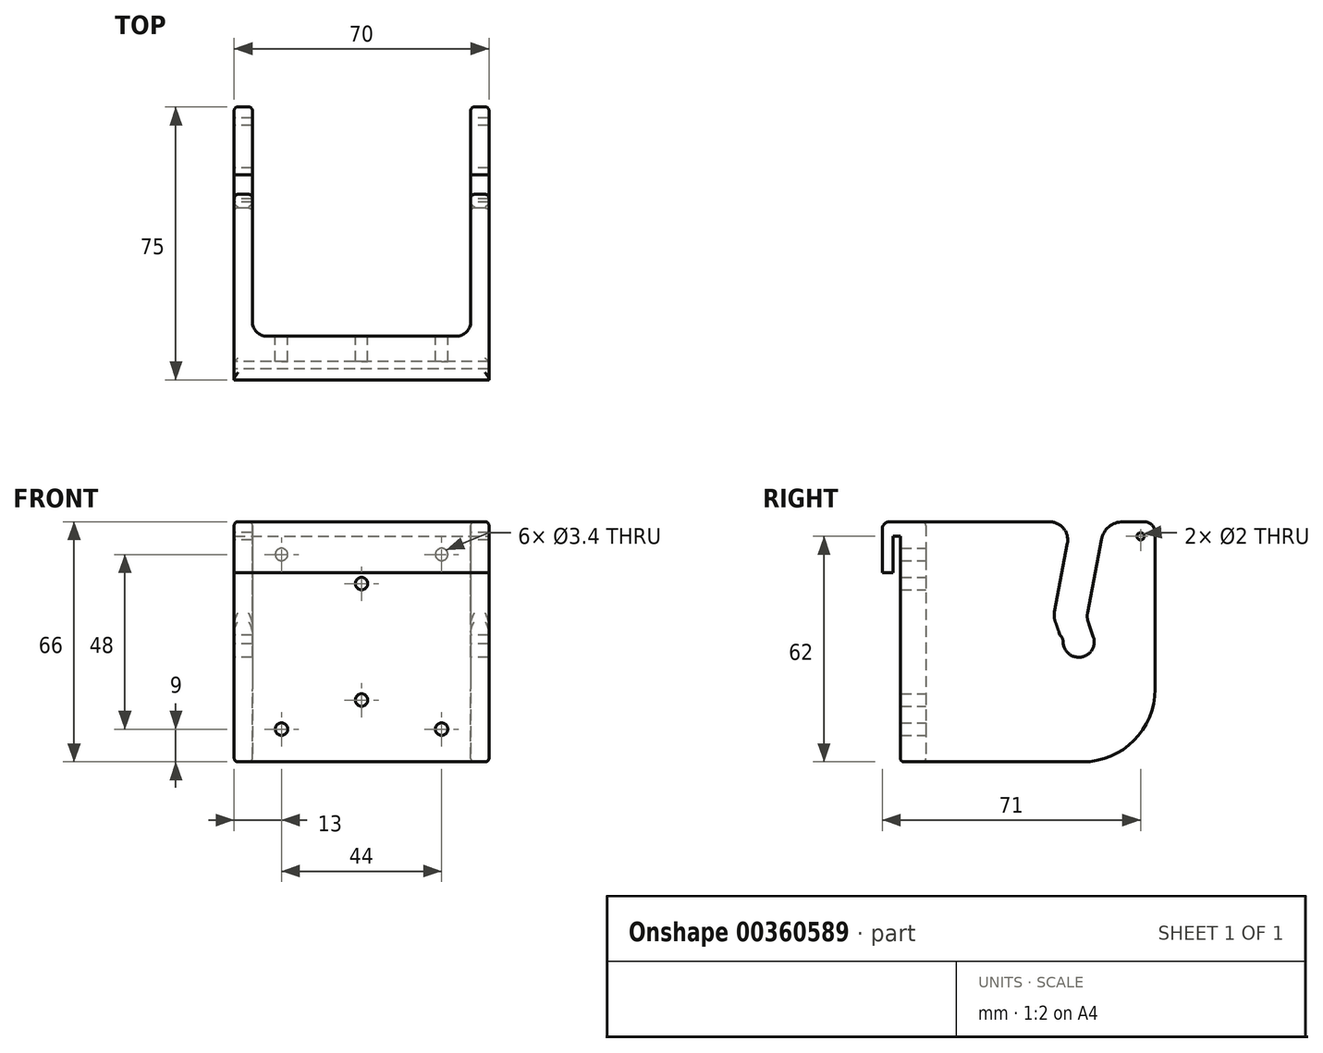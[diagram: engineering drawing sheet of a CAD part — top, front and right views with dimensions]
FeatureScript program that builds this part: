
annotation { "Feature Type Name" : "Feature", "Feature Type Description" : "" }
export const myFeature = defineFeature(function(context is Context, id is Id, definition is map)
    precondition{}
    {
        {
            var Q0;
            Q0=qCreatedBy(makeId("Right.planeOp"),FACE);
            var sketch = newSketch(context, id + "F0", { "sketchPlane" : qUnion([Q0])});
            skLineSegment(sketch, "E0.bottom", {"start": v(0, 0) * mm, "end": v(50, 0) * mm});
            skLineSegment(sketch, "E0.left", {"start": v(0, 0) * mm, "end": v(0, 66) * mm});
            skLineSegment(sketch, "E0.right", {"start": v(70, 20) * mm, "end": v(70, 63) * mm});
            skLineSegment(sketch, "E1", {"start": v(49, 33) * mm, "end": v(0, 33) * mm, "construction": true});
            skCircle(sketch, "E2", {"center": v(66, 62) * mm, "radius": 1 * mm});
            skPoint(sketch, "E3.visualSharp", {"position": v(70, 0) * mm});
            skArc(sketch, "E3.filletArc", {"start": v(50, 0) * mm, "mid": v(64.14, 5.86) * mm, "end": v(70, 20) * mm});
            skPoint(sketch, "E4.visualSharp", {"position": v(70, 70) * mm});
            skArc(sketch, "E4.filletArc", {"start": v(70, 63) * mm, "mid": v(69.12, 65.12) * mm, "end": v(67, 66) * mm});
            skLineSegment(sketch, "E5", {"start": v(67, 66) * mm, "end": v(61.13, 66) * mm});
            skArc(sketch, "E6", {"start": v(44.99, 31.6) * mm, "mid": v(50.4, 28.99) * mm, "end": v(53.01, 34.4) * mm});
            skLineSegment(sketch, "E7", {"start": v(42.52, 38.7) * mm, "end": v(43.84, 34.89) * mm});
            skLineSegment(sketch, "E8", {"start": v(51.62, 38.4) * mm, "end": v(53.01, 34.4) * mm});
            skLineSegment(sketch, "E9", {"start": v(42.32, 41.27) * mm, "end": v(45.88, 60.07) * mm});
            skLineSegment(sketch, "E10", {"start": v(51.43, 40.97) * mm, "end": v(55.24, 61.11) * mm});
            skPoint(sketch, "E11.orphan", {"position": v(33, 66) * mm});
            skPoint(sketch, "E12.orphan", {"position": v(42, 66) * mm});
            skLineSegment(sketch, "E13.trimOffspring", {"start": v(40.97, 66) * mm, "end": v(0, 66) * mm});
            skPoint(sketch, "E14.visualSharp", {"position": v(42.08, 39.95) * mm});
            skArc(sketch, "E14.filletArc", {"start": v(42.32, 41.27) * mm, "mid": v(42.25, 39.97) * mm, "end": v(42.52, 38.7) * mm});
            skPoint(sketch, "E15.visualSharp", {"position": v(51.18, 39.66) * mm});
            skArc(sketch, "E15.filletArc", {"start": v(51.43, 40.97) * mm, "mid": v(51.35, 39.67) * mm, "end": v(51.62, 38.4) * mm});
            skPoint(sketch, "E16.visualSharp", {"position": v(56.16, 66) * mm});
            skArc(sketch, "E16.filletArc", {"start": v(61.13, 66) * mm, "mid": v(57.3, 64.62) * mm, "end": v(55.24, 61.11) * mm});
            skPoint(sketch, "E17.visualSharp", {"position": v(47, 66) * mm});
            skArc(sketch, "E17.filletArc", {"start": v(45.88, 60.07) * mm, "mid": v(44.82, 64.2) * mm, "end": v(40.97, 66) * mm});
            skCircle(sketch, "E18", {"center": v(49, 33) * mm, "radius": 33 * mm, "construction": true});
            skCircle(sketch, "E19", {"center": v(49, 33) * mm, "radius": 4.25 * mm, "construction": true});
            skArc(sketch, "E20", {"start": v(44.7, 32.42) * mm, "mid": v(44.6, 33.77) * mm, "end": v(43.84, 34.89) * mm});
            skLineSegment(sketch, "E21.trimOffspring", {"start": v(44.7, 32.42) * mm, "end": v(44.99, 31.6) * mm});
            skSolve(sketch);
        }
        {
            var Q0;
            Q0=qSketchRegion(id+"F0",true);
            extrude(context, id + "F1", {"entities" : qUnion([Q0]), "depth" : 70 * mm});
        }
        {
            var Q0;
            Q0=makeQuery(id+"F1.opExtrude","SWEPT_FACE",FACE,{"disambiguationData":[OSD([sQuery(id+"F0.wireOp",EDGE,"E0.right")])]});
            var sketch = newSketch(context, id + "F2", { "sketchPlane" : qUnion([Q0])});
            skLineSegment(sketch, "E22.left", {"start": v(-65, 89.13) * mm, "end": v(-65, -5.87) * mm});
            skLineSegment(sketch, "E23", {"start": v(-35, 20) * mm, "end": v(-35, 82.42) * mm, "construction": true});
            skLineSegment(sketch, "E24.MirrorCS", {"start": v(-5, 89.13) * mm, "end": v(-5, -5.87) * mm});
            skLineSegment(sketch, "E25", {"start": v(-65, 89.13) * mm, "end": v(-5, 89.13) * mm});
            skLineSegment(sketch, "E26", {"start": v(-5, -5.87) * mm, "end": v(-65, -5.87) * mm});
            skSolve(sketch);
        }
        {
            var Q0;
            Q0=qSketchRegion(id+"F2",true);
            extrude(context, id + "F3", {"entities" : qUnion([Q0]), "operationType" : NewBodyOperationType.REMOVE, "oppositeDirection" : true, "depth" : 63 * mm});
        }
        {
            var Q0;
            Q0=makeQuery(id+"F3.boolean.opBoolean","COPY",FACE,{"derivedFrom":makeQuery(id+"F3.opExtrude","CAP_FACE",FACE,{"disambiguationData":[OSD([sQuery(id+"F2.wireOp",EDGE,"E22.left"),sQuery(id+"F2.wireOp",EDGE,"E24.MirrorCS"),sQuery(id+"F2.wireOp",EDGE,"E25"),sQuery(id+"F2.wireOp",EDGE,"E26")])],"isStart":false})});
            var sketch = newSketch(context, id + "F4", { "sketchPlane" : qUnion([Q0])});
            skLineSegment(sketch, "E27", {"start": v(-35, 66) * mm, "end": v(-35, 0) * mm, "construction": true});
            skLineSegment(sketch, "E28", {"start": v(-35, 33) * mm, "end": v(-91, 33) * mm, "construction": true});
            skPoint(sketch, "E28.endSnap0", {"position": v(-65, 33) * mm});
            skCircle(sketch, "E29", {"center": v(-57, 57) * mm, "radius": 1.7 * mm});
            skCircle(sketch, "E30", {"center": v(-57, 9) * mm, "radius": 1.7 * mm});
            skCircle(sketch, "E31.MirrorC", {"center": v(-13, 9) * mm, "radius": 1.7 * mm});
            skCircle(sketch, "E32.MirrorC", {"center": v(-13, 57) * mm, "radius": 1.7 * mm});
            skCircle(sketch, "E33", {"center": v(-35, 49) * mm, "radius": 1.7 * mm});
            skCircle(sketch, "E34.MirrorC", {"center": v(-35, 17) * mm, "radius": 1.7 * mm});
            skSolve(sketch);
        }
        {
            var Q0;
            Q0=qSketchRegion(id+"F4",true);
            extrude(context, id + "F5", {"entities" : qUnion([Q0]), "operationType" : NewBodyOperationType.REMOVE, "endBound" : BoundingType.THROUGH_ALL, "oppositeDirection" : true, "depth" : 25 * mm});
        }
        {
            var Q0;
            Q0=makeQuery(id+"F3.boolean.opBoolean","COPY",EDGE,{"derivedFrom":makeQuery(id+"F3.opExtrude","CAP_EDGE",EDGE,{"disambiguationData":[OSD([sQuery(id+"F2.wireOp",EDGE,"E22.left")])],"isStart":false})});
            var Q1;
            Q1=makeQuery(id+"F3.boolean.opBoolean","COPY",EDGE,{"derivedFrom":makeQuery(id+"F3.opExtrude","CAP_EDGE",EDGE,{"disambiguationData":[OSD([sQuery(id+"F2.wireOp",EDGE,"E24.MirrorCS")])],"isStart":false})});
            fillet(context, id + "F6", {"entities" : qUnion([Q0, Q1]), "radius" : 4 * mm, "tangentPropagation" : true, "allowEdgeOverflow" : false});
        }
        {
            var Q0;
            Q0=makeQuery(id+"F1.opExtrude","SWEPT_FACE",FACE,{"disambiguationData":[OSD([sQuery(id+"F0.wireOp",EDGE,"E0.left")])]});
            var sketch = newSketch(context, id + "F7", { "sketchPlane" : qUnion([Q0])});
            skLineSegment(sketch, "E35.bottom", {"start": v(0, 66) * mm, "end": v(70, 66) * mm});
            skLineSegment(sketch, "E35.top", {"start": v(0, 52) * mm, "end": v(70, 52) * mm});
            skLineSegment(sketch, "E35.left", {"start": v(0, 66) * mm, "end": v(0, 52) * mm});
            skLineSegment(sketch, "E35.right", {"start": v(70, 66) * mm, "end": v(70, 52) * mm});
            skSolve(sketch);
        }
        {
            var Q0;
            Q0 = qSketchRegion(id + "F7", true);
            extrude(context, id + "F8", {"entities" : qUnion([Q0]), "operationType" : NewBodyOperationType.ADD, "depth" : 5 * mm});
        }
        {
            var Q0;
            Q0=makeQuery(id+"F8.opExtrude","SWEPT_FACE",FACE,{"disambiguationData":[OSD([sQuery(id+"F7.wireOp",EDGE,"E35.top")])]});
            var sketch = newSketch(context, id + "F9", { "sketchPlane" : qUnion([Q0])});
            skLineSegment(sketch, "E36.bottom", {"start": v(70, 0) * mm, "end": v(0, 0) * mm});
            skLineSegment(sketch, "E36.top", {"start": v(70, 2) * mm, "end": v(0, 2) * mm});
            skLineSegment(sketch, "E36.left", {"start": v(70, 0) * mm, "end": v(70, 2) * mm});
            skLineSegment(sketch, "E36.right", {"start": v(0, 0) * mm, "end": v(0, 2) * mm});
            skSolve(sketch);
        }
        {
            var Q0;
            Q0 = qSketchRegion(id + "F9", true);
            extrude(context, id + "F10", {"entities" : qUnion([Q0]), "operationType" : NewBodyOperationType.REMOVE, "oppositeDirection" : true, "depth" : 10 * mm});
        }
        {
            var Q0;
            Q0=makeQuery(id+"F8.opExtrude","CAP_EDGE",EDGE,{"disambiguationData":[OSD([sQuery(id+"F7.wireOp",EDGE,"E35.bottom")])],"isStart":false});
            fillet(context, id + "F11", {"entities" : qUnion([Q0]), "radius" : 2 * mm, "tangentPropagation" : true, "allowEdgeOverflow" : false});
        }
        {
            var Q0;
            Q0=makeQuery(id+"F8.boolean.opBoolean","MERGE",FACE,{"derivedFrom":[makeQuery(id+"F1.opExtrude","SWEPT_FACE",FACE,{"disambiguationData":[OSD([sQuery(id+"F0.wireOp",EDGE,"E13.trimOffspring")])]}),makeQuery(id+"F8.opExtrude","SWEPT_FACE",FACE,{"disambiguationData":[OSD([sQuery(id+"F7.wireOp",EDGE,"E35.bottom")])]})]});
            var Q1;
            {var subQ0=sQuery(id+"F0.wireOp",EDGE,"E17.filletArc");Q1=makeQuery(id+"F3.boolean.opBoolean","SPLIT",FACE,{"disambiguationData":[TD([makeQuery(id+"F3.opExtrude","SWEPT_FACE",FACE,{"disambiguationData":[OSD([sQuery(id+"F2.wireOp",EDGE,"E24.MirrorCS")])]})])],"derivedFrom":makeQuery(id+"F1.opExtrude","SWEPT_FACE",FACE,{"disambiguationData":[OSD([subQ0])]})});}
            var Q2;
            {var subQ0=sQuery(id+"F0.wireOp",EDGE,"E17.filletArc");Q2=makeQuery(id+"F3.boolean.opBoolean","SPLIT",FACE,{"disambiguationData":[TD([makeQuery(id+"F3.opExtrude","SWEPT_FACE",FACE,{"disambiguationData":[OSD([sQuery(id+"F2.wireOp",EDGE,"E22.left")])]})])],"derivedFrom":makeQuery(id+"F1.opExtrude","SWEPT_FACE",FACE,{"disambiguationData":[OSD([subQ0])]})});}
            var Q3;
            {var subQ2=sQuery(id+"F0.wireOp",EDGE,"E9");Q3=makeQuery(id+"F3.boolean.opBoolean","SPLIT",FACE,{"disambiguationData":[TD([makeQuery(id+"F3.opExtrude","SWEPT_FACE",FACE,{"disambiguationData":[OSD([sQuery(id+"F2.wireOp",EDGE,"E22.left")])]})])],"derivedFrom":makeQuery(id+"F1.opExtrude","SWEPT_FACE",FACE,{"disambiguationData":[OSD([subQ2])]})});}
            var Q4;
            {var subQ2=sQuery(id+"F0.wireOp",EDGE,"E9");Q4=makeQuery(id+"F3.boolean.opBoolean","SPLIT",FACE,{"disambiguationData":[TD([makeQuery(id+"F3.opExtrude","SWEPT_FACE",FACE,{"disambiguationData":[OSD([sQuery(id+"F2.wireOp",EDGE,"E24.MirrorCS")])]})])],"derivedFrom":makeQuery(id+"F1.opExtrude","SWEPT_FACE",FACE,{"disambiguationData":[OSD([subQ2])]})});}
            var Q5;
            {var subQ0=sQuery(id+"F0.wireOp",EDGE,"E14.filletArc");Q5=makeQuery(id+"F3.boolean.opBoolean","SPLIT",FACE,{"disambiguationData":[TD([makeQuery(id+"F3.opExtrude","SWEPT_FACE",FACE,{"disambiguationData":[OSD([sQuery(id+"F2.wireOp",EDGE,"E24.MirrorCS")])]})])],"derivedFrom":makeQuery(id+"F1.opExtrude","SWEPT_FACE",FACE,{"disambiguationData":[OSD([subQ0])]})});}
            var Q6;
            {var subQ0=sQuery(id+"F0.wireOp",EDGE,"E14.filletArc");Q6=makeQuery(id+"F3.boolean.opBoolean","SPLIT",FACE,{"disambiguationData":[TD([makeQuery(id+"F3.opExtrude","SWEPT_FACE",FACE,{"disambiguationData":[OSD([sQuery(id+"F2.wireOp",EDGE,"E22.left")])]})])],"derivedFrom":makeQuery(id+"F1.opExtrude","SWEPT_FACE",FACE,{"disambiguationData":[OSD([subQ0])]})});}
            var Q7;
            {var subQ2=sQuery(id+"F0.wireOp",EDGE,"E0.right");Q7=makeQuery(id+"F3.boolean.opBoolean","SPLIT",FACE,{"disambiguationData":[TD([makeQuery(id+"F3.opExtrude","SWEPT_FACE",FACE,{"disambiguationData":[OSD([sQuery(id+"F2.wireOp",EDGE,"E22.left")])]})])],"derivedFrom":makeQuery(id+"F1.opExtrude","SWEPT_FACE",FACE,{"disambiguationData":[OSD([subQ2])]})});}
            var Q8;
            {var subQ2=sQuery(id+"F0.wireOp",EDGE,"E0.right");Q8=makeQuery(id+"F3.boolean.opBoolean","SPLIT",FACE,{"disambiguationData":[TD([makeQuery(id+"F3.opExtrude","SWEPT_FACE",FACE,{"disambiguationData":[OSD([sQuery(id+"F2.wireOp",EDGE,"E24.MirrorCS")])]})])],"derivedFrom":makeQuery(id+"F1.opExtrude","SWEPT_FACE",FACE,{"disambiguationData":[OSD([subQ2])]})});}
            var Q9;
            {var subQ1=sQuery(id+"F0.wireOp",EDGE,"E4.filletArc");Q9=makeQuery(id+"F3.boolean.opBoolean","SPLIT",FACE,{"disambiguationData":[TD([makeQuery(id+"F3.opExtrude","SWEPT_FACE",FACE,{"disambiguationData":[OSD([sQuery(id+"F2.wireOp",EDGE,"E22.left")])]})])],"derivedFrom":makeQuery(id+"F1.opExtrude","SWEPT_FACE",FACE,{"disambiguationData":[OSD([subQ1])]})});}
            var Q10;
            {var subQ1=sQuery(id+"F0.wireOp",EDGE,"E5");Q10=makeQuery(id+"F3.boolean.opBoolean","SPLIT",FACE,{"disambiguationData":[TD([makeQuery(id+"F3.opExtrude","SWEPT_FACE",FACE,{"disambiguationData":[OSD([sQuery(id+"F2.wireOp",EDGE,"E22.left")])]})])],"derivedFrom":makeQuery(id+"F1.opExtrude","SWEPT_FACE",FACE,{"disambiguationData":[OSD([subQ1])]})});}
            var Q11;
            {var subQ0=sQuery(id+"F0.wireOp",EDGE,"E16.filletArc");Q11=makeQuery(id+"F3.boolean.opBoolean","SPLIT",FACE,{"disambiguationData":[TD([makeQuery(id+"F3.opExtrude","SWEPT_FACE",FACE,{"disambiguationData":[OSD([sQuery(id+"F2.wireOp",EDGE,"E22.left")])]})])],"derivedFrom":makeQuery(id+"F1.opExtrude","SWEPT_FACE",FACE,{"disambiguationData":[OSD([subQ0])]})});}
            var Q12;
            {var subQ2=sQuery(id+"F0.wireOp",EDGE,"E10");Q12=makeQuery(id+"F3.boolean.opBoolean","SPLIT",FACE,{"disambiguationData":[TD([makeQuery(id+"F3.opExtrude","SWEPT_FACE",FACE,{"disambiguationData":[OSD([sQuery(id+"F2.wireOp",EDGE,"E22.left")])]})])],"derivedFrom":makeQuery(id+"F1.opExtrude","SWEPT_FACE",FACE,{"disambiguationData":[OSD([subQ2])]})});}
            var Q13;
            {var subQ2=sQuery(id+"F0.wireOp",EDGE,"E10");Q13=makeQuery(id+"F3.boolean.opBoolean","SPLIT",FACE,{"disambiguationData":[TD([makeQuery(id+"F3.opExtrude","SWEPT_FACE",FACE,{"disambiguationData":[OSD([sQuery(id+"F2.wireOp",EDGE,"E24.MirrorCS")])]})])],"derivedFrom":makeQuery(id+"F1.opExtrude","SWEPT_FACE",FACE,{"disambiguationData":[OSD([subQ2])]})});}
            var Q14;
            {var subQ0=sQuery(id+"F0.wireOp",EDGE,"E16.filletArc");Q14=makeQuery(id+"F3.boolean.opBoolean","SPLIT",FACE,{"disambiguationData":[TD([makeQuery(id+"F3.opExtrude","SWEPT_FACE",FACE,{"disambiguationData":[OSD([sQuery(id+"F2.wireOp",EDGE,"E24.MirrorCS")])]})])],"derivedFrom":makeQuery(id+"F1.opExtrude","SWEPT_FACE",FACE,{"disambiguationData":[OSD([subQ0])]})});}
            var Q15;
            {var subQ1=sQuery(id+"F0.wireOp",EDGE,"E5");Q15=makeQuery(id+"F3.boolean.opBoolean","SPLIT",FACE,{"disambiguationData":[TD([makeQuery(id+"F3.opExtrude","SWEPT_FACE",FACE,{"disambiguationData":[OSD([sQuery(id+"F2.wireOp",EDGE,"E24.MirrorCS")])]})])],"derivedFrom":makeQuery(id+"F1.opExtrude","SWEPT_FACE",FACE,{"disambiguationData":[OSD([subQ1])]})});}
            var Q16;
            {var subQ1=sQuery(id+"F0.wireOp",EDGE,"E3.filletArc");Q16=makeQuery(id+"F3.boolean.opBoolean","SPLIT",FACE,{"disambiguationData":[TD([makeQuery(id+"F3.opExtrude","SWEPT_FACE",FACE,{"disambiguationData":[OSD([sQuery(id+"F2.wireOp",EDGE,"E22.left")])]})])],"derivedFrom":makeQuery(id+"F1.opExtrude","SWEPT_FACE",FACE,{"disambiguationData":[OSD([subQ1])]})});}
            var Q17;
            {var subQ1=sQuery(id+"F0.wireOp",EDGE,"E3.filletArc");Q17=makeQuery(id+"F3.boolean.opBoolean","SPLIT",FACE,{"disambiguationData":[TD([makeQuery(id+"F3.opExtrude","SWEPT_FACE",FACE,{"disambiguationData":[OSD([sQuery(id+"F2.wireOp",EDGE,"E24.MirrorCS")])]})])],"derivedFrom":makeQuery(id+"F1.opExtrude","SWEPT_FACE",FACE,{"disambiguationData":[OSD([subQ1])]})});}
            var Q18;
            {var subQ1=sQuery(id+"F0.wireOp",EDGE,"E4.filletArc");Q18=makeQuery(id+"F3.boolean.opBoolean","SPLIT",FACE,{"disambiguationData":[TD([makeQuery(id+"F3.opExtrude","SWEPT_FACE",FACE,{"disambiguationData":[OSD([sQuery(id+"F2.wireOp",EDGE,"E24.MirrorCS")])]})])],"derivedFrom":makeQuery(id+"F1.opExtrude","SWEPT_FACE",FACE,{"disambiguationData":[OSD([subQ1])]})});}
            var Q19;
            Q19=makeQuery(id+"F1.opExtrude","SWEPT_FACE",FACE,{"disambiguationData":[OSD([sQuery(id+"F0.wireOp",EDGE,"E0.bottom")])]});
            var Q20;
            {var subQ0=sQuery(id+"F0.wireOp",EDGE,"E15.filletArc");Q20=makeQuery(id+"F3.boolean.opBoolean","SPLIT",FACE,{"disambiguationData":[TD([makeQuery(id+"F3.opExtrude","SWEPT_FACE",FACE,{"disambiguationData":[OSD([sQuery(id+"F2.wireOp",EDGE,"E24.MirrorCS")])]})])],"derivedFrom":makeQuery(id+"F1.opExtrude","SWEPT_FACE",FACE,{"disambiguationData":[OSD([subQ0])]})});}
            var Q21;
            {var subQ0=sQuery(id+"F0.wireOp",EDGE,"E15.filletArc");Q21=makeQuery(id+"F3.boolean.opBoolean","SPLIT",FACE,{"disambiguationData":[TD([makeQuery(id+"F3.opExtrude","SWEPT_FACE",FACE,{"disambiguationData":[OSD([sQuery(id+"F2.wireOp",EDGE,"E22.left")])]})])],"derivedFrom":makeQuery(id+"F1.opExtrude","SWEPT_FACE",FACE,{"disambiguationData":[OSD([subQ0])]})});}
            fillet(context, id + "F12", {"entities" : qUnion([Q0, Q1, Q2, Q3, Q4, Q5, Q6, Q7, Q8, Q9, Q10, Q11, Q12, Q13, Q14, Q15, Q16, Q17, Q18, Q19, Q20, Q21]), "radius" : 1 * mm, "allowEdgeOverflow" : false});
        }
    });
